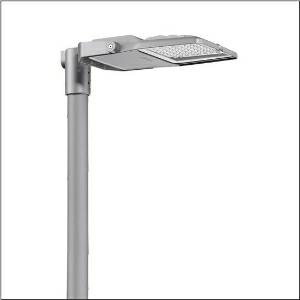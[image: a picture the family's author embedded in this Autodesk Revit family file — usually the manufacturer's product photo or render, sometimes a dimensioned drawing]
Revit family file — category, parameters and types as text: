
# Revit family: floodlight_fl_21_iq_mini___pl52_5xa7772b4d3a_2373
name_source: partatom
category: Lighting Fixtures
units: mm (PartAtom-declared; Revit-internal decimal feet)

## family parameters
Cut with Voids When Loaded = No
Host = Face
Light Source = No
Part Type = Normal
Room Calculation Point = No
Round Connector Dimension = Use Diameter
Shared = No

## types (1)
- --- (1 x LED, 6490 lm, 45.5 W, 4000K)
    Apparent Load = 46 VA
    CIE Flux Codes = 26 60 98 100 100
    Color Rendering = 70
    Color Temperature = 4000K
    Default Elevation = 1800 mm
    Description = Floodlight FL 21 iQ mini, floodlight, primary light control with lens, of PMMA, primary optical cover: protective disc, of toughened safety glass, transparent, light distribution: PL52, light emission: direct distribution, installation type: surface-mounted, LED, High Power LED, rated luminous flux: 6.490lm, luminous efficacy: 143lm/W, light colour: 740, colour temperature: 4000K, control gear: iQ Street-Remote/DALI, control: Auto-Match, Temp-Guard, Night-Set, Smart-Wire, Desk-Remote (wireless, voltage-free reading and setting of iQ features in the workshop via application-optimized NFC function/RFID function), optimised constant luminous flux control (CLO 2.0), Light-Fading, Lumen-Switch, with terminal, 6-pole, mains connection: 220..240V, AC, 50/60Hz, start of lifetime: 46W, end of service life: 48W, reduction: 22W, luminaire housing, of diecast aluminium, powder-coated, Siteco® metallic grey (DB 702S), corrosivity category C5 mid according to DIN EN ISO 12944, suitable for swimming pools, chlorine-resistant, sealing non-destructively replaceable, please order mast flange separately, mast bracket, of steel, galvanised, powder-coated, protection rating (complete): IP66, insulation class (complete): insulation class II (safety insulation), certification: CE, ENEC, VDE, protection symbol: D, impact resistance: IK08, permissible operating ambient temperature: -40..+40°C, permissible operating ambient temperature for outdoor applications: -40..+50°C, standard: DIN EN 12944, LABS conformity tested according to VDMA 24364:2018-05, packaging unit: 1 piece

Light Distribution: PL52
    Height = 70 mm
    Lamp = 1 x LED
    Lamp Light Flux = 6490 lm
    Lamp Power = 45.5 W
    Lamp count = 1
    Length = 485 mm
    Luminous efficacy = 143 lm/W
    Manufacturer = Siteco
    ModVariant = No
    Model = 5XA7772B4D3A
    Number of Poles = 1
    OnlyDefault = Yes
    Power Factor = 1
    Product Name = Floodlight FL 21 iQ mini | PL52
    Product group = floodlight | pylon annexe
    ProductGroupID = 6200
    Protection Class = Protection class II
    Protection Degree = IP 66
    RLX_Detail_Level = 1
    RLX_Emergency_Light_Flux = 0 lm
    RLX_Emergency_Type = 0
    RLX_Emergency_Type_DB = No
    RlxData = <blob elided: 101533 chars, md5=78ccb85e>
    Socket = socket
    Standby Power = 0 W
    System Light Flux = 6490 lm
    System Power = 46 W
    Type Comments = factory setting: luminous flux: 100 % | dim-lin: 254 | 463 mA
    Type Image = l_1007125.jpg
    URL = http://relux.com
    VarID = @adj_164700
    Voltage = 0 V
    Weight = 0.00 kg
    Width = 337 mm

## geometry (parser evidence)
native form markers: Blend x4, Sweep x12
no freeform markers — native parametric forms only
